# Revit family: Hook_Strip-Stainless_Steel-Bobrick-B-232
name_source: partatom
category: Specialty Equipment
units: mm (PartAtom-declared; Revit-internal decimal feet)

## family parameters
Cut with Voids When Loaded = No
Host = Face
OmniClass Number = 23.40.20.21.31
OmniClass Title = Robe Hooks
Part Type = Normal
Room Calculation Point = No
Round Connector Dimension = Use Diameter
Shared = No

## types (1)
- B-232 x 24
    ADA Compliant = No
    ADA Elevation = 48"
    ADA Height = 60"
    Assembly Code = C1030320
    CL to CL = 10 1/2"
    Default Elevation = 20"
    Description = Surface-Mounted Hook Strip, Satin Finish
    Elevation Height = 60"
    Finish = Stainless Steel-Bobrick-Type 304-Satin
    Installation Type = Wall-Mounted
    Manufacturer = Bobrick Washroom Equipment, Inc.
    Material = Stainless Steel-Bobrick-Type 304-Satin
    Model = B-232 x 24
    Not ADA = Yes
    Product Documentation Link = https://www.bobrick.com
    Product Page URL = https://www.bobrick.com
    Recommended Height = Yes
    Revised Date = 10/22/2024
    URL = http://www.bobrick.com
    Unit Depth = 2 1/4"
    Unit Height = 6 1/2"
    Unit Length = 24"

## geometry (parser evidence)
native form markers: Sweep x3
no freeform markers — native parametric forms only
